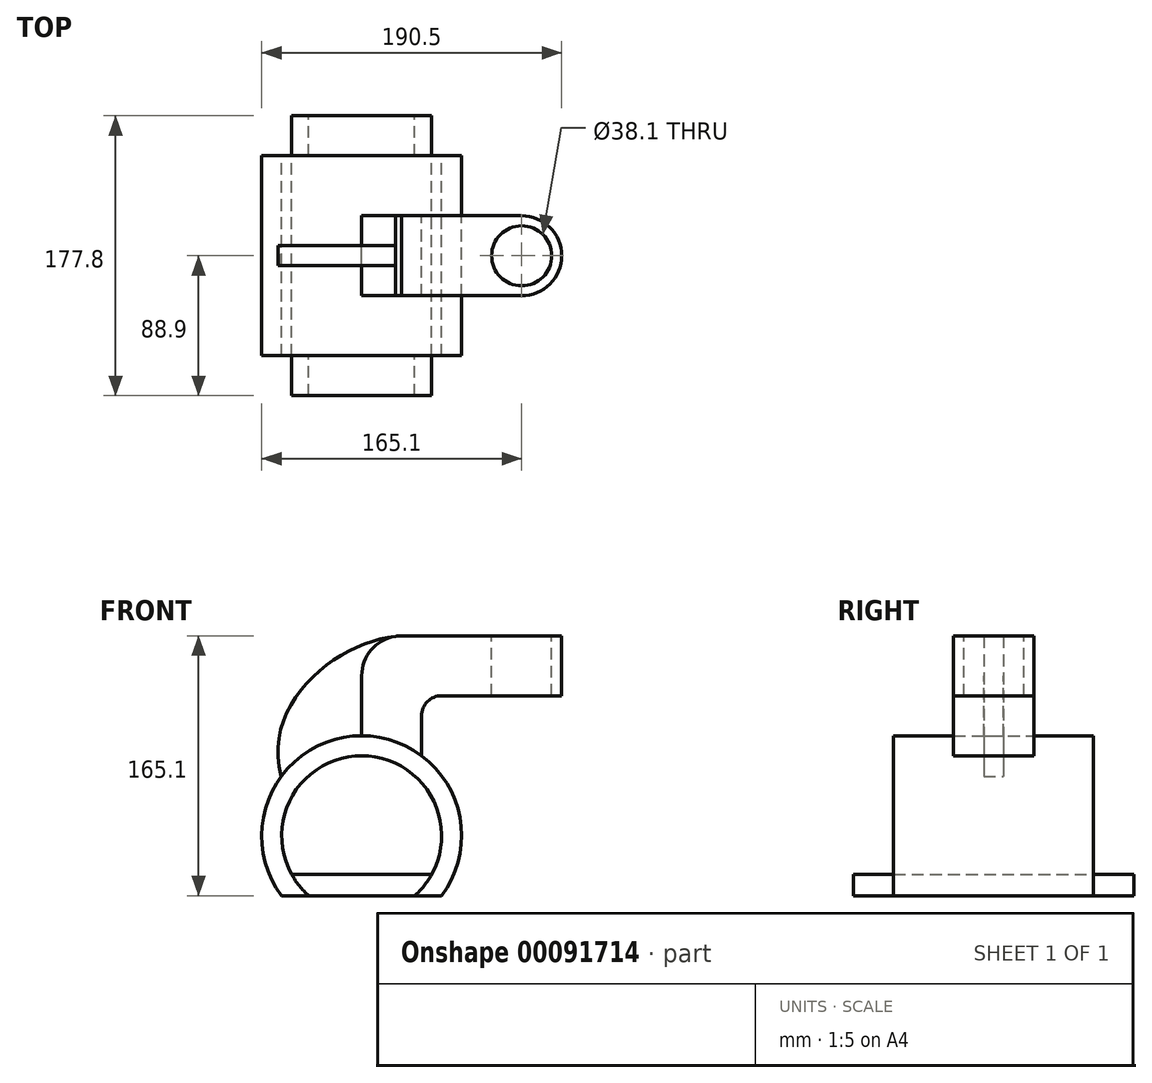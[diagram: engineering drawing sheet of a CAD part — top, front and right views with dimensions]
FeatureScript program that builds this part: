
annotation { "Feature Type Name" : "Feature", "Feature Type Description" : "" }
export const myFeature = defineFeature(function(context is Context, id is Id, definition is map)
    precondition{}
    {
        {
            var Q0;
            Q0=qCreatedBy(makeId("Front.planeOp"),FACE);
            var sketch = newSketch(context, id + "F0", { "sketchPlane" : qUnion([Q0])});
            skCircle(sketch, "E0", {"center": v(0, 0) * mm, "radius": 63.5 * mm});
            skLineSegment(sketch, "E1", {"start": v(-50.8, -38.1) * mm, "end": v(50.8, -38.1) * mm});
            skLineSegment(sketch, "E2.bottom", {"start": v(127, 88.9) * mm, "end": v(76.2, 88.9) * mm});
            skLineSegment(sketch, "E2.top", {"start": v(127, 127) * mm, "end": v(76.2, 127) * mm});
            skLineSegment(sketch, "E2.left", {"start": v(127, 88.9) * mm, "end": v(127, 127) * mm});
            skLineSegment(sketch, "E2.right", {"start": v(76.2, 88.9) * mm, "end": v(76.2, 127) * mm});
            skPoint(sketch, "E2.middle", {"position": v(101.6, 107.95) * mm});
            skLineSegment(sketch, "E3", {"start": v(38.1, 50.8) * mm, "end": v(38.1, 76.2) * mm});
            skLineSegment(sketch, "E4", {"start": v(76.2, 88.9) * mm, "end": v(50.8, 88.9) * mm});
            skArc(sketch, "E5", {"start": v(50.8, 88.9) * mm, "mid": v(41.82, 85.18) * mm, "end": v(38.1, 76.2) * mm});
            skLineSegment(sketch, "E6", {"start": v(76.2, 127) * mm, "end": v(25.4, 127) * mm});
            skLineSegment(sketch, "E7", {"start": v(0, 63.5) * mm, "end": v(0, 101.6) * mm});
            skArc(sketch, "E8", {"start": v(25.4, 127) * mm, "mid": v(7.44, 119.56) * mm, "end": v(0, 101.6) * mm});
            skLineSegment(sketch, "E9", {"start": v(101.6, 127) * mm, "end": v(101.6, 88.9) * mm});
            skFitSpline(sketch, "E10", {"points": [v(25.4, 127) * mm, v(-51.18, 37.6) * mm], "startDerivative": vector(-107.9, -4.87) * mm, "endDerivative": vector(39.08, -152.13) * mm});
            skCircle(sketch, "E11", {"center": v(0, 0) * mm, "radius": 50.8 * mm});
            skLineSegment(sketch, "E12", {"start": v(-44.45, -24.6) * mm, "end": v(44.45, -24.6) * mm});
            skSolve(sketch);
        }
        {
            var Q0;
            {var subQ3=sQuery(id+"F0.wireOp",EDGE,"E1");Q0=makeQuery(id+"F0.imprint","IMPRINT",FACE,{"disambiguationData":[TD([[makeQuery(id+"F0.imprint","IMPRINT",EDGE,{"derivedFrom":subQ3}),1.0]])]});}
            extrude(context, id + "F1", {"entities" : qUnion([Q0]), "endBound" : BoundingType.SYMMETRIC, "depth" : 127 * mm});
        }
        {
            var Q0;
            Q0=makeQuery(id+"F0.imprint","IMPRINT",FACE,{"disambiguationData":[TD([[makeQuery(id+"F0.imprint","IMPRINT",EDGE,{"derivedFrom":sQuery(id+"F0.wireOp",EDGE,"E2.right")}),1.0]])]});
            var Q1;
            {var subQ0=sQuery(id+"F0.wireOp",EDGE,"E2.right");Q1=makeQuery(id+"F0.imprint","IMPRINT",FACE,{"disambiguationData":[TD([[makeQuery(id+"F0.imprint","IMPRINT",EDGE,{"derivedFrom":subQ0}),-1.0]])]});}
            extrude(context, id + "F2", {"entities" : qUnion([Q0, Q1]), "endBound" : BoundingType.SYMMETRIC, "depth" : 50.8 * mm});
        }
        {
            var Q0;
            {var subQ0=sQuery(id+"F0.wireOp",EDGE,"E7");Q0=makeQuery(id+"F0.imprint","IMPRINT",FACE,{"disambiguationData":[TD([[makeQuery(id+"F0.imprint","IMPRINT",EDGE,{"derivedFrom":subQ0}),1.0]])]});}
            extrude(context, id + "F3", {"entities" : qUnion([Q0]), "endBound" : BoundingType.SYMMETRIC, "depth" : 12.7 * mm});
        }
        {
            var Q0;
            {var subQ0=sQuery(id+"F0.wireOp",EDGE,"E2.left");Q0=makeQuery(id+"F0.imprint","IMPRINT",FACE,{"disambiguationData":[TD([[makeQuery(id+"F0.imprint","IMPRINT",EDGE,{"derivedFrom":subQ0}),1.0]])]});}
            var Q1;
            Q1=sQuery(id+"F0.wireOp",EDGE,"E9");
            revolve(context, id + "F4", {"operationType" : NewBodyOperationType.ADD, "entities" : qUnion([Q0]), "axis" : qUnion([Q1]), "revolveType" : RevolveType.SYMMETRIC, "angle" : 180 * degree});
        }
        {
            var Q0;
            {var subQ4=sQuery(id+"F0.wireOp",EDGE,"E12");Q0=makeQuery(id+"F0.imprint","IMPRINT",FACE,{"disambiguationData":[TD([[makeQuery(id+"F0.imprint","IMPRINT",EDGE,{"derivedFrom":subQ4}),-1.0]])]});}
            extrude(context, id + "F5", {"entities" : qUnion([Q0]), "operationType" : NewBodyOperationType.ADD, "endBound" : BoundingType.SYMMETRIC, "depth" : 177.8 * mm});
        }
        {
            var Q0;
            {var subQ0=sQuery(id+"F0.wireOp",EDGE,"E2.top");Q0=makeQuery(id+"F4.boolean.opBoolean","MERGE",FACE,{"derivedFrom":[makeQuery(id+"F2.opExtrude","SWEPT_FACE",FACE,{"disambiguationData":[OSD([subQ0,sQuery(id+"F0.wireOp",EDGE,"E6")])]}),makeQuery(id+"F4.opRevolve","SWEPT_FACE",FACE,{"disambiguationData":[OSD([subQ0])]})]});}
            var sketch = newSketch(context, id + "F6", { "sketchPlane" : qUnion([Q0])});
            skCircle(sketch, "E13", {"center": v(101.6, 0) * mm, "radius": 19.05 * mm});
            skSolve(sketch);
        }
        {
            var Q0;
            Q0=makeQuery(id+"F6.imprint","IMPRINT",FACE,{"disambiguationData":[TD([[makeQuery(id+"F6.imprint","IMPRINT",EDGE,{"derivedFrom":sQuery(id+"F6.wireOp",EDGE,"E13")}),1.0]])]});
            extrude(context, id + "F7", {"entities" : qUnion([Q0]), "operationType" : NewBodyOperationType.REMOVE, "oppositeDirection" : true, "depth" : 50.8 * mm});
        }
    });
